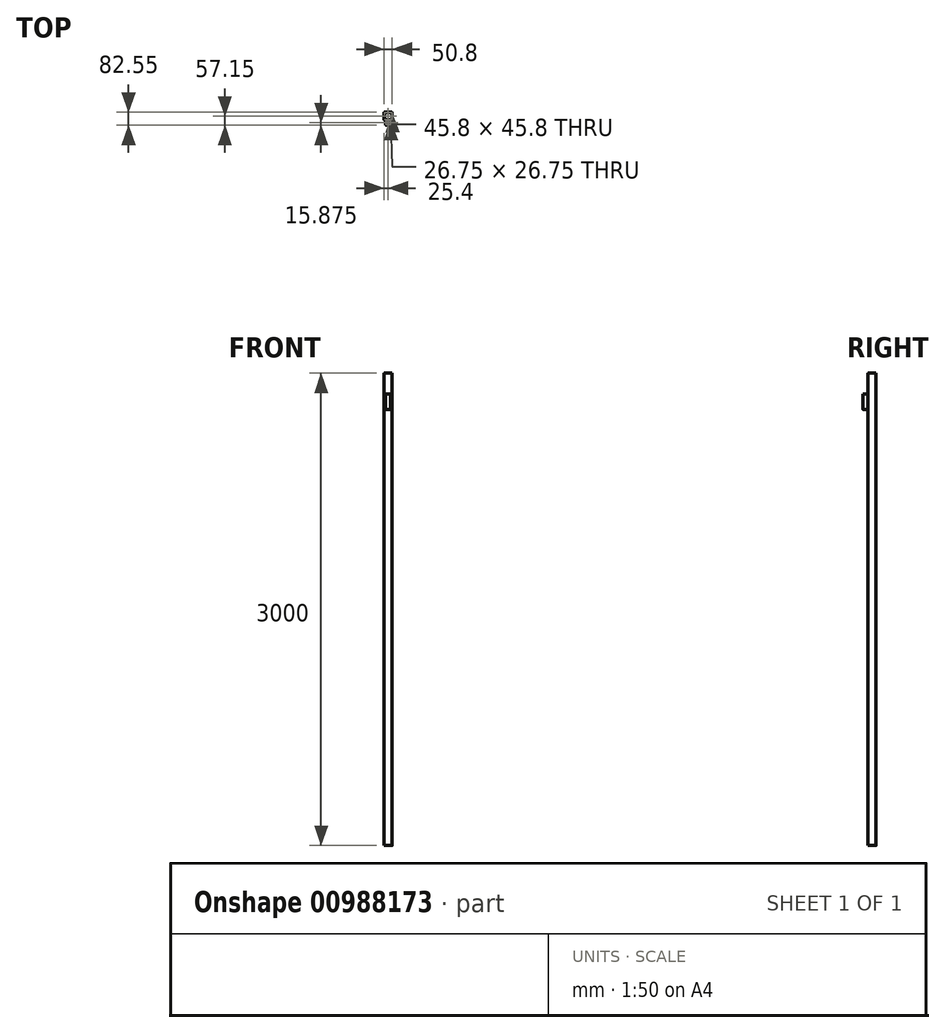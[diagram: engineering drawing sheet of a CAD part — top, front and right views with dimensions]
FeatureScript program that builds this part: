
annotation { "Feature Type Name" : "Feature", "Feature Type Description" : "" }
export const myFeature = defineFeature(function(context is Context, id is Id, definition is map)
    precondition{}
    {
        {
            var Q0;
            Q0=qCreatedBy(makeId("Top.planeOp"),FACE);
            var sketch = newSketch(context, id + "F0", { "sketchPlane" : qUnion([Q0])});
            skLineSegment(sketch, "E0.bottom", {"start": v(22.9, 25.4) * mm, "end": v(-22.9, 25.4) * mm});
            skLineSegment(sketch, "E0.top", {"start": v(22.9, -25.4) * mm, "end": v(-22.9, -25.4) * mm});
            skLineSegment(sketch, "E0.left", {"start": v(25.4, 22.9) * mm, "end": v(25.4, -22.9) * mm});
            skLineSegment(sketch, "E0.right", {"start": v(-25.4, 22.9) * mm, "end": v(-25.4, -22.9) * mm});
            skPoint(sketch, "E0.middle", {"position": v(0, 0) * mm});
            skPoint(sketch, "E1.visualSharp", {"position": v(25.4, 25.4) * mm});
            skArc(sketch, "E1.filletArc", {"start": v(25.4, 22.9) * mm, "mid": v(24.67, 24.67) * mm, "end": v(22.9, 25.4) * mm});
            skPoint(sketch, "E2.visualSharp", {"position": v(-25.4, 25.4) * mm});
            skArc(sketch, "E2.filletArc", {"start": v(-22.9, 25.4) * mm, "mid": v(-24.67, 24.67) * mm, "end": v(-25.4, 22.9) * mm});
            skPoint(sketch, "E3.visualSharp", {"position": v(-25.4, -25.4) * mm});
            skArc(sketch, "E3.filletArc", {"start": v(-25.4, -22.9) * mm, "mid": v(-24.67, -24.67) * mm, "end": v(-22.9, -25.4) * mm});
            skPoint(sketch, "E4.visualSharp", {"position": v(25.4, -25.4) * mm});
            skArc(sketch, "E4.filletArc", {"start": v(22.9, -25.4) * mm, "mid": v(24.67, -24.67) * mm, "end": v(25.4, -22.9) * mm});
            skLineSegment(sketch, "E5.0", {"start": v(22.9, 22.9) * mm, "end": v(22.9, 22.9) * mm});
            skLineSegment(sketch, "E5.1", {"start": v(22.9, 22.9) * mm, "end": v(22.9, -22.9) * mm});
            skLineSegment(sketch, "E5.2", {"start": v(22.9, 22.9) * mm, "end": v(-22.9, 22.9) * mm});
            skLineSegment(sketch, "E5.3", {"start": v(22.9, -22.9) * mm, "end": v(22.9, -22.9) * mm});
            skLineSegment(sketch, "E5.4", {"start": v(-22.9, 22.9) * mm, "end": v(-22.9, 22.9) * mm});
            skLineSegment(sketch, "E5.5", {"start": v(-22.9, 22.9) * mm, "end": v(-22.9, -22.9) * mm});
            skLineSegment(sketch, "E5.6", {"start": v(-22.9, -22.9) * mm, "end": v(-22.9, -22.9) * mm});
            skLineSegment(sketch, "E5.7", {"start": v(22.9, -22.9) * mm, "end": v(-22.9, -22.9) * mm});
            skSolve(sketch);
        }
        {
            var Q0;
            Q0=makeQuery(id+"F0.imprint","IMPRINT",FACE,{"disambiguationData":[TD([[makeQuery(id+"F0.imprint","IMPRINT",EDGE,{"derivedFrom":sQuery(id+"F0.wireOp",EDGE,"E0.bottom")}),1.0]])]});
            extrude(context, id + "F1", {"entities" : qUnion([Q0]), "depth" : 3000 * mm, "offsetDistance" : 25 * mm});
        }
        {
            var Q0;
            Q0=makeQuery(id+"F1.opExtrude","SWEPT_FACE",FACE,{"disambiguationData":[OSD([sQuery(id+"F0.wireOp",EDGE,"E0.top")])]});
            var sketch = newSketch(context, id + "F2", { "sketchPlane" : qUnion([Q0])});
            skLineSegment(sketch, "E6.bottom", {"start": v(15.88, 2868.25) * mm, "end": v(-15.87, 2868.25) * mm});
            skLineSegment(sketch, "E6.top", {"start": v(15.88, 2768.25) * mm, "end": v(-15.87, 2768.25) * mm});
            skLineSegment(sketch, "E6.left", {"start": v(15.88, 2868.25) * mm, "end": v(15.88, 2768.25) * mm});
            skLineSegment(sketch, "E6.right", {"start": v(-15.87, 2868.25) * mm, "end": v(-15.87, 2768.25) * mm});
            skPoint(sketch, "E6.middle", {"position": v(0, 2818.25) * mm});
            skSolve(sketch);
        }
        {
            var Q0;
            Q0 = qSketchRegion(id + "F2", true);
            extrude(context, id + "F3", {"entities" : qUnion([Q0]), "operationType" : NewBodyOperationType.ADD, "depth" : 31.75 * mm, "offsetDistance" : 25 * mm});
        }
        {
            var Q0;
            Q0=makeQuery(id+"F3.opExtrude","CAP_EDGE",EDGE,{"disambiguationData":[OSD([sQuery(id+"F2.wireOp",EDGE,"E6.right")])],"isStart":false});
            var Q1;
            Q1=makeQuery(id+"F3.opExtrude","CAP_EDGE",EDGE,{"disambiguationData":[OSD([sQuery(id+"F2.wireOp",EDGE,"E6.left")])],"isStart":false});
            fillet(context, id + "F4", {"entities" : qUnion([Q0, Q1]), "radius" : 2.5 * mm, "tangentPropagation" : true, "allowEdgeOverflow" : false});
        }
        {
            var Q0;
            Q0=makeQuery(id+"F3.opExtrude","SWEPT_FACE",FACE,{"disambiguationData":[OSD([sQuery(id+"F2.wireOp",EDGE,"E6.bottom")])]});
            var sketch = newSketch(context, id + "F5", { "sketchPlane" : qUnion([Q0])});
            skLineSegment(sketch, "E7.0", {"start": v(13.38, -54.65) * mm, "end": v(13.38, -27.9) * mm});
            skLineSegment(sketch, "E7.1", {"start": v(-13.37, -54.65) * mm, "end": v(-13.37, -27.9) * mm});
            skLineSegment(sketch, "E7.2", {"start": v(-13.37, -54.65) * mm, "end": v(-13.37, -54.65) * mm});
            skLineSegment(sketch, "E7.3", {"start": v(13.38, -27.9) * mm, "end": v(-13.37, -27.9) * mm});
            skLineSegment(sketch, "E7.4", {"start": v(13.38, -54.65) * mm, "end": v(-13.37, -54.65) * mm});
            skLineSegment(sketch, "E7.5", {"start": v(13.38, -54.65) * mm, "end": v(13.38, -54.65) * mm});
            skSolve(sketch);
        }
        {
            var Q0;
            Q0 = qSketchRegion(id + "F5", true);
            extrude(context, id + "F6", {"entities" : qUnion([Q0]), "operationType" : NewBodyOperationType.REMOVE, "endBound" : BoundingType.UP_TO_NEXT, "oppositeDirection" : true, "depth" : 25 * mm, "offsetDistance" : 25 * mm});
        }
        {
            var Q0;
            Q0=qCreatedBy(makeId("Front.planeOp"),FACE);
            var sketch = newSketch(context, id + "F7", { "sketchPlane" : qUnion([Q0])});
            skLineSegment(sketch, "E8", {"start": v(0, 0) * mm, "end": v(0, 52.75) * mm});
            skSolve(sketch);
        }
    });
